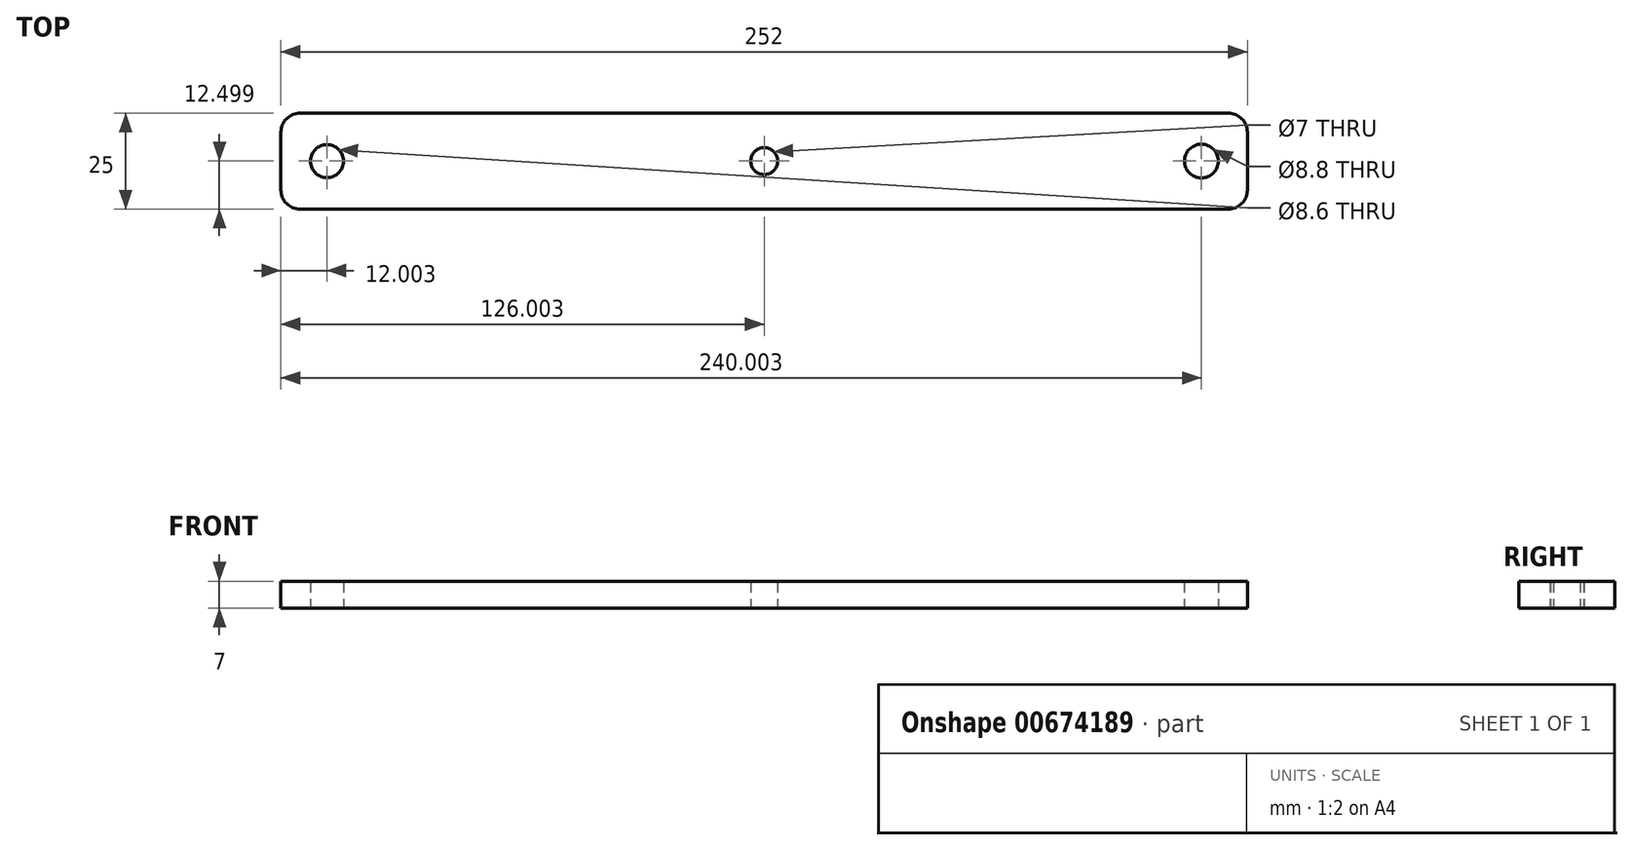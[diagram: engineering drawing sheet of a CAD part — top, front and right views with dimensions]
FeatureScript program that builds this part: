
annotation { "Feature Type Name" : "Feature", "Feature Type Description" : "" }
export const myFeature = defineFeature(function(context is Context, id is Id, definition is map)
    precondition{}
    {
        {
            var Q0;
            Q0=qCreatedBy(makeId("Top.planeOp"),FACE);
            var sketch = newSketch(context, id + "F0", { "sketchPlane" : qUnion([Q0])});
            skLineSegment(sketch, "E0.bottom", {"start": v(-137.8, -4.06) * mm, "end": v(114.2, -4.06) * mm});
            skLineSegment(sketch, "E0.top", {"start": v(-137.8, -29.06) * mm, "end": v(114.2, -29.06) * mm});
            skLineSegment(sketch, "E0.left", {"start": v(-137.8, -4.06) * mm, "end": v(-137.8, -29.06) * mm});
            skLineSegment(sketch, "E0.right", {"start": v(114.2, -4.06) * mm, "end": v(114.2, -29.06) * mm});
            skLineSegment(sketch, "E1", {"start": v(-11.8, -4.06) * mm, "end": v(-11.8, -29.06) * mm, "construction": true});
            skCircle(sketch, "E2", {"center": v(-11.8, -16.56) * mm, "radius": 3.5 * mm});
            skLineSegment(sketch, "E3", {"start": v(-11.8, -16.56) * mm, "end": v(102.2, -16.56) * mm, "construction": true});
            skCircle(sketch, "E4", {"center": v(102.2, -16.56) * mm, "radius": 4.4 * mm});
            skLineSegment(sketch, "E5", {"start": v(-11.8, -16.56) * mm, "end": v(-125.8, -16.56) * mm, "construction": true});
            skCircle(sketch, "E6", {"center": v(-125.8, -16.56) * mm, "radius": 4.3 * mm});
            skSolve(sketch);
        }
        {
            var Q0;
            Q0=makeQuery(id+"F0.imprint","IMPRINT",FACE,{"disambiguationData":[TD([[makeQuery(id+"F0.imprint","IMPRINT",EDGE,{"derivedFrom":sQuery(id+"F0.wireOp",EDGE,"E0.bottom")}),-1.0]])]});
            extrude(context, id + "F1", {"entities" : qUnion([Q0]), "depth" : 7 * mm, "offsetDistance" : 25 * mm});
        }
        {
            var Q0;
            Q0=makeQuery(id+"F1.opExtrude","SWEPT_EDGE",EDGE,{"disambiguationData":[OSD([sQuery(id+"F0.wireOp",EDGE,"E0.top"),sQuery(id+"F0.wireOp",EDGE,"E0.right")])]});
            var Q1;
            Q1=makeQuery(id+"F1.opExtrude","SWEPT_EDGE",EDGE,{"disambiguationData":[OSD([sQuery(id+"F0.wireOp",EDGE,"E0.bottom"),sQuery(id+"F0.wireOp",EDGE,"E0.right")])]});
            var Q2;
            Q2=makeQuery(id+"F1.opExtrude","SWEPT_EDGE",EDGE,{"disambiguationData":[OSD([sQuery(id+"F0.wireOp",EDGE,"E0.top"),sQuery(id+"F0.wireOp",EDGE,"E0.left")])]});
            var Q3;
            Q3=makeQuery(id+"F1.opExtrude","SWEPT_EDGE",EDGE,{"disambiguationData":[OSD([sQuery(id+"F0.wireOp",EDGE,"E0.bottom"),sQuery(id+"F0.wireOp",EDGE,"E0.left")])]});
            fillet(context, id + "F2", {"entities" : qUnion([Q0, Q1, Q2, Q3]), "radius" : 5 * mm, "tangentPropagation" : true, "allowEdgeOverflow" : false});
        }
    });
